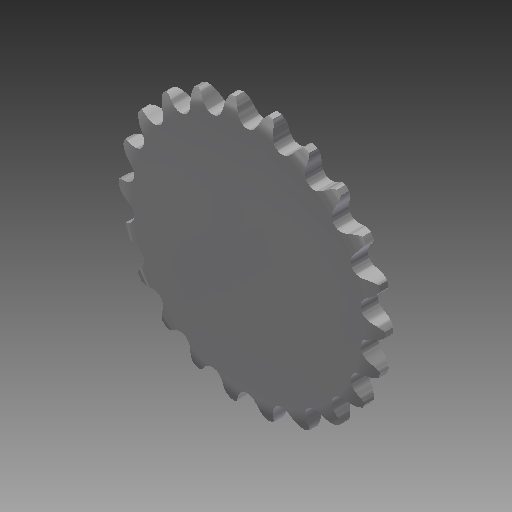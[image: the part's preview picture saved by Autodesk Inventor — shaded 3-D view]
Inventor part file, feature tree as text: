
AUTODESK INVENTOR PART (.ipt)
format: ipt  version: 2017 (Build 210142000, 142)  size: 615,936 bytes
history: native  units: mm
features: other x6, extrude x2, pattern_linear x1, pattern_circular x1
ambient origin geometry x8: Origin, YZ Plane, XZ Plane, XY Plane, X Axis, Y Axis, Z Axis, Center Point
bodies: Solid1 (feature_tree)
feature tree (10):
  other  "Theoretical Tooth Profile"
  other  "Tooth Profile"
  other  "Section Profile"
  other  "Shroud"
  other  "Strand"
  pattern_linear  "Strand Pattern"  Spacing1=44.619381mm  [1 undecoded]
  extrude  "Theoretical Tooth"  Depth=2.855993mm
  extrude  "Tooth"  Depth=1.697355mm
  pattern_circular  "Tooth Pattern"  [2 undecoded]
  other  "Timing Plane"
note: 3 required parameter values undecoded (feature->parameter linkage not recoverable at this tier; creation-order binding heuristic only, values carry confidence <= 0.55)
